# Revit family: BVL2x2_2x4
name_source: partatom
category: Lighting Fixtures
units: mm (PartAtom-declared; Revit-internal decimal feet)

## family parameters
Always vertical = Yes
Cut with Voids When Loaded = No
Host = Ceiling
Light Source = Yes
OmniClass Number = 23.80.70.11.14.17
OmniClass Title = Direct/Indirect
Part Type = Normal
Room Calculation Point = No
Round Connector Dimension = Use Diameter
Shared = No

## types (10) — shared parameters
Assembly Code = D5020200
Color Filter = 16777215
Description = Architectural Recessed Troffer
Dimming Lamp Color Temperature Shift = <None>
Emit Shape Visible in Rendering = No
Emit from Rectangle Height = 0' - 0 1/32"
Emit from Rectangle Width = 1' - 11 3/4"
Housing Finish = Metal - Viscor - White
Lamp = LED
Lens Depth = 0' - 0 1/32"
Lens Finish = Acrylic - Viscor - Frosted White
Manufacturer = VISIONEERING by VISCOR
Model = BVL
Tilt Angle = 90.00°
URL = https://www.viscor.com
Voltage = 120 V
Width = 1' - 11 3/4"

## per-type parameters (varying)
| type | Apparent Load | Emit from Rectangle Length | Lamp Wattage | Length | Photometric Web File |
| BVL2X2-LED840K035LUNV | 30 VA | 1' - 11 3/4" | 30 VA | 1' - 11 3/4" | BVL2X2-LED840K035LUNV.ies |
| BVL2X4-LED840K042LUNV | 34 VA | 3' - 11 3/4" | 34 VA | 3' - 11 3/4" | BVL2X4-LED840K042LUNV.ies |
| BVL2X2-LED840K025LUNV | 21 VA | 1' - 11 3/4" | 21 VA | 1' - 11 3/4" | BVL2X2-LED840K025LUNV.ies |
| BVL2X2-LED840K042LUNV | 37 VA | 1' - 11 3/4" | 37 VA | 1' - 11 3/4" | BVL2X2-LED840K042LUNV.ies |
| BVL2X2-LED840K050LUNV | 43 VA | 1' - 11 3/4" | 43 VA | 1' - 11 3/4" | BVL2X2-LED840K050LUNV.ies |
| BVL2X4-LED840K025LUNV | 21 VA | 3' - 11 3/4" | 21 VA | 3' - 11 3/4" | BVL2X4-LED840K025LUNV.ies |
| BVL2X4-LED840K035LUNV | 28 VA | 3' - 11 3/4" | 28 VA | 3' - 11 3/4" | BVL2X4-LED840K035LUNV.ies |
| BVL2X4-LED840K050LUNV | 41 VA | 3' - 11 3/4" | 41 VA | 3' - 11 3/4" | BVL2X4-LED840K050LUNV.ies |
| BVL2X4-LED840K060LUNV | 50 VA | 3' - 11 3/4" | 50 VA | 3' - 11 3/4" | BVL2X4-LED840K060LUNV.ies |
| BVL2X4-LED840K070LUNV | 60 VA | 3' - 11 3/4" | 60 VA | 3' - 11 3/4" | BVL2X4-LED840K070LUNV.ies |

## geometry (parser evidence)
native form markers: Sweep x2
no freeform markers — native parametric forms only
